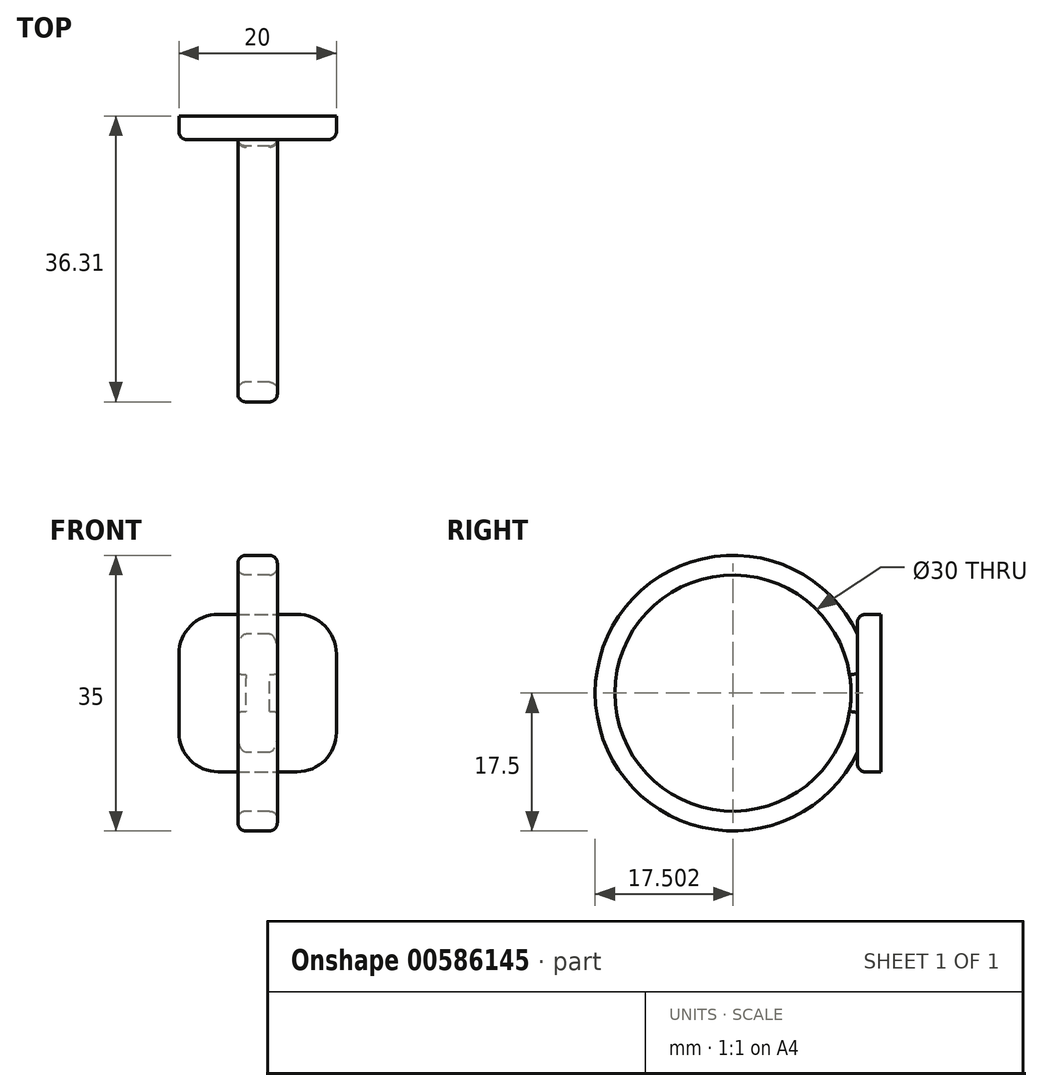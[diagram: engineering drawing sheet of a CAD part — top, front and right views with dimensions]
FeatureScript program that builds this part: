
annotation { "Feature Type Name" : "Feature", "Feature Type Description" : "" }
export const myFeature = defineFeature(function(context is Context, id is Id, definition is map)
    precondition{}
    {
        {
            var Q0;
            Q0=qCreatedBy(makeId("Front.planeOp"),FACE);
            var sketch = newSketch(context, id + "F0", { "sketchPlane" : qUnion([Q0])});
            skLineSegment(sketch, "E0.bottom", {"start": v(-10, 10) * mm, "end": v(10, 10) * mm});
            skLineSegment(sketch, "E0.top", {"start": v(-10, -10) * mm, "end": v(10, -10) * mm});
            skLineSegment(sketch, "E0.left", {"start": v(-10, 10) * mm, "end": v(-10, -10) * mm});
            skLineSegment(sketch, "E0.right", {"start": v(10, 10) * mm, "end": v(10, -10) * mm});
            skPoint(sketch, "E0.middle", {"position": v(0, 0) * mm});
            skSolve(sketch);
        }
        {
            var Q0;
            Q0 = qSketchRegion(id + "F0", true);
            extrude(context, id + "F1", {"entities" : qUnion([Q0]), "depth" : (3) * mm, "offsetDistance" : 25 * mm});
        }
        {
            var Q0;
            Q0=qCreatedBy(makeId("Right.planeOp"),FACE);
            var sketch = newSketch(context, id + "F2", { "sketchPlane" : qUnion([Q0])});
            skCircle(sketch, "E1", {"center": v(-18.8, 0) * mm, "radius": 17.5 * mm});
            skCircle(sketch, "E2", {"center": v(-18.8, 0) * mm, "radius": 15 * mm});
            skSolve(sketch);
        }
        {
            var Q0;
            Q0=makeQuery(id+"F2.imprint","IMPRINT",FACE,{"disambiguationData":[TD([[makeQuery(id+"F2.imprint","IMPRINT",EDGE,{"derivedFrom":sQuery(id+"F2.wireOp",EDGE,"E1")}),1.0]])]});
            extrude(context, id + "F3", {"entities" : qUnion([Q0]), "operationType" : NewBodyOperationType.ADD, "endBound" : BoundingType.SYMMETRIC, "depth" : 5 * mm, "offsetDistance" : 25 * mm});
        }
        {
            var Q0;
            Q0=makeQuery(id+"F3.opExtrude","CAP_EDGE",EDGE,{"disambiguationData":[OSD([sQuery(id+"F2.wireOp",EDGE,"E1")])],"isStart":false});
            var Q1;
            Q1=makeQuery(id+"F3.opExtrude","CAP_EDGE",EDGE,{"disambiguationData":[OSD([sQuery(id+"F2.wireOp",EDGE,"E1")])],"isStart":true});
            var Q2;
            Q2=makeQuery(id+"F3.opExtrude","CAP_EDGE",EDGE,{"disambiguationData":[OSD([sQuery(id+"F2.wireOp",EDGE,"E2")])],"isStart":true});
            var Q3;
            Q3=makeQuery(id+"F3.opExtrude","CAP_EDGE",EDGE,{"disambiguationData":[OSD([sQuery(id+"F2.wireOp",EDGE,"E2")])],"isStart":false});
            var Q4;
            Q4=makeQuery(id+"F1.opExtrude","CAP_EDGE",EDGE,{"disambiguationData":[OSD([sQuery(id+"F0.wireOp",EDGE,"E0.right")])],"isStart":false});
            var Q5;
            Q5=makeQuery(id+"F1.opExtrude","CAP_EDGE",EDGE,{"disambiguationData":[OSD([sQuery(id+"F0.wireOp",EDGE,"E0.bottom")])],"isStart":false});
            var Q6;
            Q6=makeQuery(id+"F1.opExtrude","CAP_EDGE",EDGE,{"disambiguationData":[OSD([sQuery(id+"F0.wireOp",EDGE,"E0.left")])],"isStart":false});
            var Q7;
            Q7=makeQuery(id+"F1.opExtrude","CAP_EDGE",EDGE,{"disambiguationData":[OSD([sQuery(id+"F0.wireOp",EDGE,"E0.top")])],"isStart":false});
            fillet(context, id + "F4", {"entities" : qUnion([Q0, Q1, Q2, Q3, Q4, Q5, Q6, Q7]), "radius" : 1 * mm, "tangentPropagation" : true, "allowEdgeOverflow" : false});
        }
        {
            var Q0;
            Q0=makeQuery(id+"F1.opExtrude","SWEPT_EDGE",EDGE,{"disambiguationData":[OSD([sQuery(id+"F0.wireOp",EDGE,"E0.bottom"),sQuery(id+"F0.wireOp",EDGE,"E0.left")])]});
            var Q1;
            Q1=makeQuery(id+"F1.opExtrude","SWEPT_EDGE",EDGE,{"disambiguationData":[OSD([sQuery(id+"F0.wireOp",EDGE,"E0.top"),sQuery(id+"F0.wireOp",EDGE,"E0.left")])]});
            var Q2;
            Q2=makeQuery(id+"F1.opExtrude","SWEPT_EDGE",EDGE,{"disambiguationData":[OSD([sQuery(id+"F0.wireOp",EDGE,"E0.bottom"),sQuery(id+"F0.wireOp",EDGE,"E0.right")])]});
            var Q3;
            Q3=makeQuery(id+"F1.opExtrude","SWEPT_EDGE",EDGE,{"disambiguationData":[OSD([sQuery(id+"F0.wireOp",EDGE,"E0.top"),sQuery(id+"F0.wireOp",EDGE,"E0.right")])]});
            fillet(context, id + "F5", {"entities" : qUnion([Q0, Q1, Q2, Q3]), "radius" : 5 * mm, "tangentPropagation" : true, "allowEdgeOverflow" : false});
        }
    });
